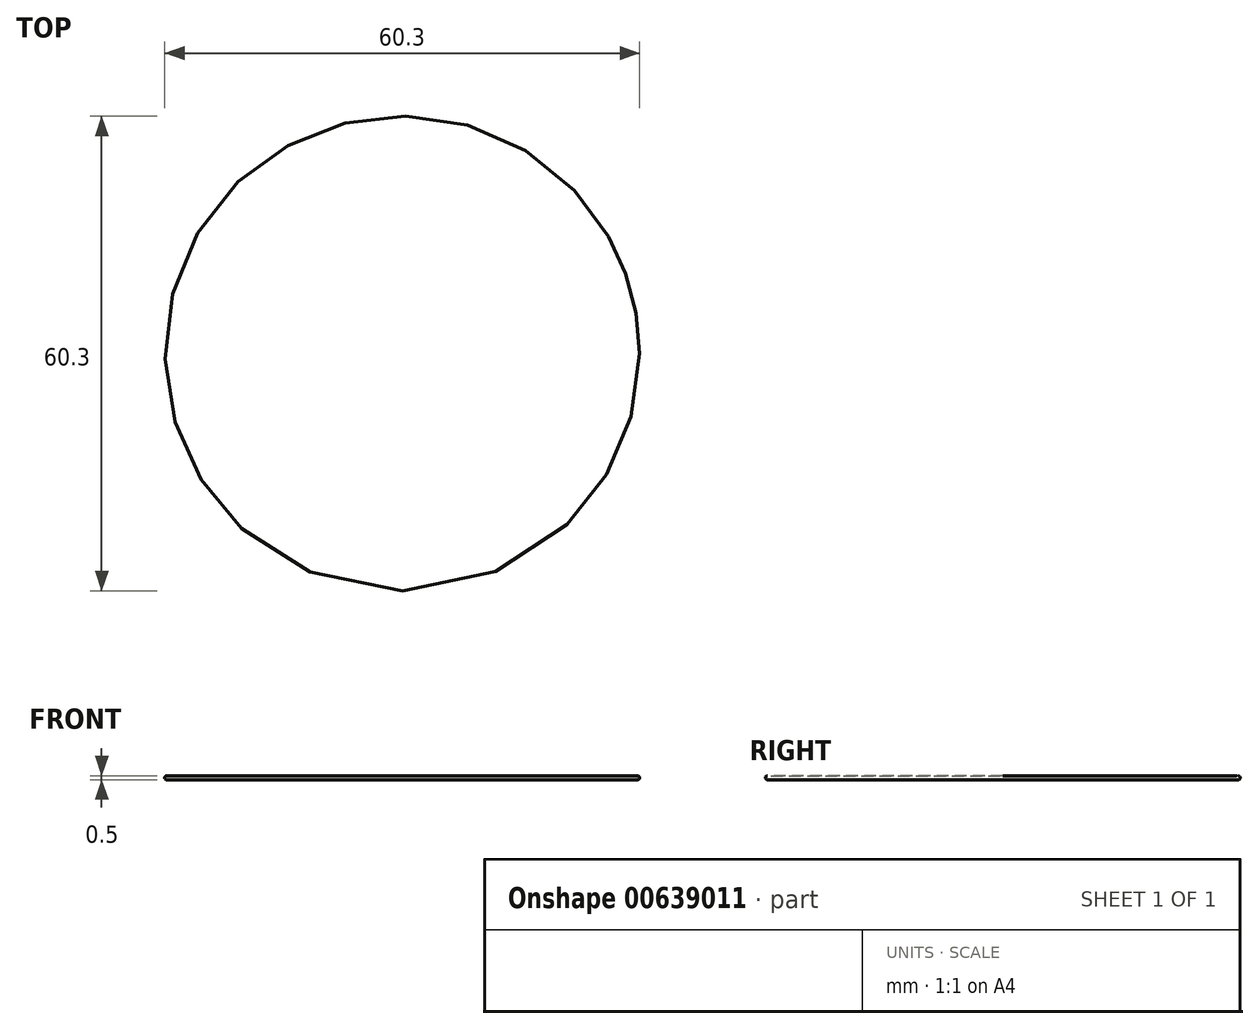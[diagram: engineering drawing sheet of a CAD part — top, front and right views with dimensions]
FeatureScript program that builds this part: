
annotation { "Feature Type Name" : "Feature", "Feature Type Description" : "" }
export const myFeature = defineFeature(function(context is Context, id is Id, definition is map)
    precondition{}
    {
        {
            var Q0;
            Q0=qCreatedBy(makeId("Front.planeOp"),FACE);
            var sketch = newSketch(context, id + "F0", { "sketchPlane" : qUnion([Q0])});
            skFitSpline(sketch, "E0", {"points": [v(-30, 52.67) * mm, v(-36.1, 45.59) * mm, v(-43.07, 30.34) * mm, v(-40.8, 14.37) * mm, v(-30, 3) * mm, v(-22.12, 0) * mm, v(-16.31, -2.95) * mm, v(-9.62, -7.63) * mm, v(-7.08, -12.56) * mm, v(-4.94, -20.04) * mm, v(-4.16, -42.1) * mm, v(-6.49, -43.46) * mm, v(-17.13, -43.27) * mm, v(-30, -43.27) * mm, v(-30, -44.81) * mm, v(-29.26, -45.5) * mm, v(-27.9, -46.53) * mm, v(-25.91, -47.33) * mm], "startDerivative": vector(-93.31, -87.25) * mm, "endDerivative": vector(65.52, -21.22) * mm});
            skLineSegment(sketch, "E1", {"start": v(-25.91, -47.33) * mm, "end": v(0, -47.33) * mm});
            skLineSegment(sketch, "E2", {"start": v(0, 52.67) * mm, "end": v(0, 52.17) * mm});
            skLineSegment(sketch, "E3", {"start": v(0, 52.17) * mm, "end": v(-30.53, 52.17) * mm});
            skFitSpline(sketch, "E4.0", {"points": [v(-30.34, 53.03) * mm, v(-31.32, 52.12) * mm, v(-32.78, 50.65) * mm, v(-34.74, 48.3) * mm, v(-36.23, 46.32) * mm, v(-37.77, 44.03) * mm, v(-39.8, 40.64) * mm, v(-41.66, 36.85) * mm, v(-43.03, 32.84) * mm, v(-43.99, 28.75) * mm, v(-44.18, 24.65) * mm, v(-43.63, 20.65) * mm, v(-42.84, 17.72) * mm, v(-41.69, 14.88) * mm, v(-40.16, 12.15) * mm, v(-38.32, 9.6) * mm, v(-36.27, 7.26) * mm, v(-34.07, 5.2) * mm, v(-32.18, 3.76) * mm, v(-30.67, 2.8) * mm, v(-29.18, 1.97) * mm, v(-27.37, 1.2) * mm, v(-25.32, 0.51) * mm, v(-23.74, 0.03) * mm, v(-22.56, -0.36) * mm, v(-21.44, -0.8) * mm, v(-20.11, -1.4) * mm, v(-18.52, -2.26) * mm, v(-16.86, -3.22) * mm, v(-15.02, -4.25) * mm, v(-13.15, -5.36) * mm, v(-11.71, -6.36) * mm, v(-10.7, -7.21) * mm, v(-10.05, -7.87) * mm, v(-9.5, -8.55) * mm, v(-8.88, -9.5) * mm, v(-8.4, -10.5) * mm, v(-8, -11.53) * mm, v(-7.7, -12.3) * mm, v(-7.42, -13.07) * mm, v(-7.14, -13.82) * mm, v(-6.86, -14.58) * mm, v(-6.48, -15.67) * mm, v(-6.11, -16.92) * mm, v(-5.75, -18.47) * mm, v(-5.48, -19.8) * mm, v(-5.22, -21.35) * mm, v(-4.88, -23.67) * mm, v(-4.5, -26.9) * mm, v(-4.16, -31) * mm, v(-4.02, -34.32) * mm, v(-4.01, -36.74) * mm, v(-4.06, -38.4) * mm, v(-4.18, -39.85) * mm, v(-4.36, -41.06) * mm, v(-4.6, -41.95) * mm, v(-4.85, -42.38) * mm, v(-5.04, -42.59) * mm, v(-5.19, -42.7) * mm, v(-5.37, -42.78) * mm, v(-5.65, -42.87) * mm, v(-6.12, -42.94) * mm, v(-6.85, -42.98) * mm, v(-7.7, -43.02) * mm, v(-8.97, -43.06) * mm, v(-10.8, -43.07) * mm, v(-12.96, -43.01) * mm, v(-14.86, -42.92) * mm, v(-16.36, -42.83) * mm, v(-17.95, -42.7) * mm, v(-19.6, -42.56) * mm, v(-21.26, -42.4) * mm, v(-22.9, -42.27) * mm, v(-24.48, -42.16) * mm, v(-25.96, -42.1) * mm, v(-27.3, -42.1) * mm, v(-28.28, -42.17) * mm, v(-28.96, -42.28) * mm, v(-29.42, -42.39) * mm, v(-29.83, -42.54) * mm, v(-30.2, -42.75) * mm, v(-30.5, -43.05) * mm, v(-30.69, -43.4) * mm, v(-30.77, -43.77) * mm, v(-30.76, -44.23) * mm, v(-30.62, -44.75) * mm, v(-30.34, -45.25) * mm, v(-30, -45.59) * mm, v(-29.73, -45.77) * mm, v(-29.54, -45.91) * mm, v(-29.39, -46.03) * mm, v(-29.22, -46.17) * mm, v(-28.97, -46.38) * mm, v(-28.7, -46.6) * mm, v(-28.4, -46.8) * mm, v(-28.15, -46.96) * mm, v(-27.9, -47.1) * mm, v(-27.55, -47.27) * mm, v(-26.94, -47.52) * mm, v(-26.4, -47.7) * mm, v(-26.06, -47.8) * mm]});
            skLineSegment(sketch, "E5.0", {"start": v(-25.91, -47.83) * mm, "end": v(0, -47.83) * mm});
            skLineSegment(sketch, "E6.0", {"start": v(0, 52.67) * mm, "end": v(-30.73, 52.67) * mm});
            skLineSegment(sketch, "E7", {"start": v(-25.91, -47.83) * mm, "end": v(-26.06, -47.8) * mm});
            skLineSegment(sketch, "E8", {"start": v(0, -47.33) * mm, "end": v(0, -47.83) * mm});
            skLineSegment(sketch, "E9", {"start": v(0, 65.29) * mm, "end": v(0, -66.25) * mm, "construction": true});
            skSolve(sketch);
        }
        {
            var Q0;
            Q0 = qSketchRegion(id + "F0", true);
            var Q1;
            Q1=sQuery(id+"F0.wireOp",EDGE,"E9");
            revolve(context, id + "F1", {"entities" : qUnion([Q0]), "axis" : qUnion([Q1]), "revolveType" : RevolveType.FULL});
        }
        {
            var Q0;
            Q0=makeQuery(id+"F1.opRevolve","SWEPT_EDGE",EDGE,{"disambiguationData":[OSD([sQuery(id+"F0.wireOp",EDGE,"E0"),sQuery(id+"F0.wireOp",EDGE,"E3")])]});
            var Q1;
            Q1=makeQuery(id+"F1.opRevolve","SWEPT_EDGE",EDGE,{"disambiguationData":[OSD([sQuery(id+"F0.wireOp",EDGE,"E4.0"),sQuery(id+"F0.wireOp",EDGE,"E6.0")])]});
            fillet(context, id + "F2", {"entities" : qUnion([Q0, Q1]), "radius" : .25 * mm, "tangentPropagation" : true, "allowEdgeOverflow" : false});
        }
        {
            var Q0;
            Q0=qCreatedBy(makeId("Front.planeOp"),FACE);
            var sketch = newSketch(context, id + "F3", { "sketchPlane" : qUnion([Q0])});
            skText(sketch, "E10", { "text": "Happy Anniversary ", "fontName": "DroidSansMono.ttf"});
            const initialGuessF3  = {"E10": [-0.03, 0.04238, 1, 0, 0.00419]};
            skSetInitialGuess(sketch, initialGuessF3);
            skSolve(sketch);
        }
        {
            var Q0;
            Q0 = qSketchRegion(id + "F3", true);
            extrude(context, id + "F4", {"entities" : qUnion([Q0]), "operationType" : NewBodyOperationType.REMOVE, "depth" : 50.3 * mm, "offsetDistance" : 25 * mm});
        }
    });
